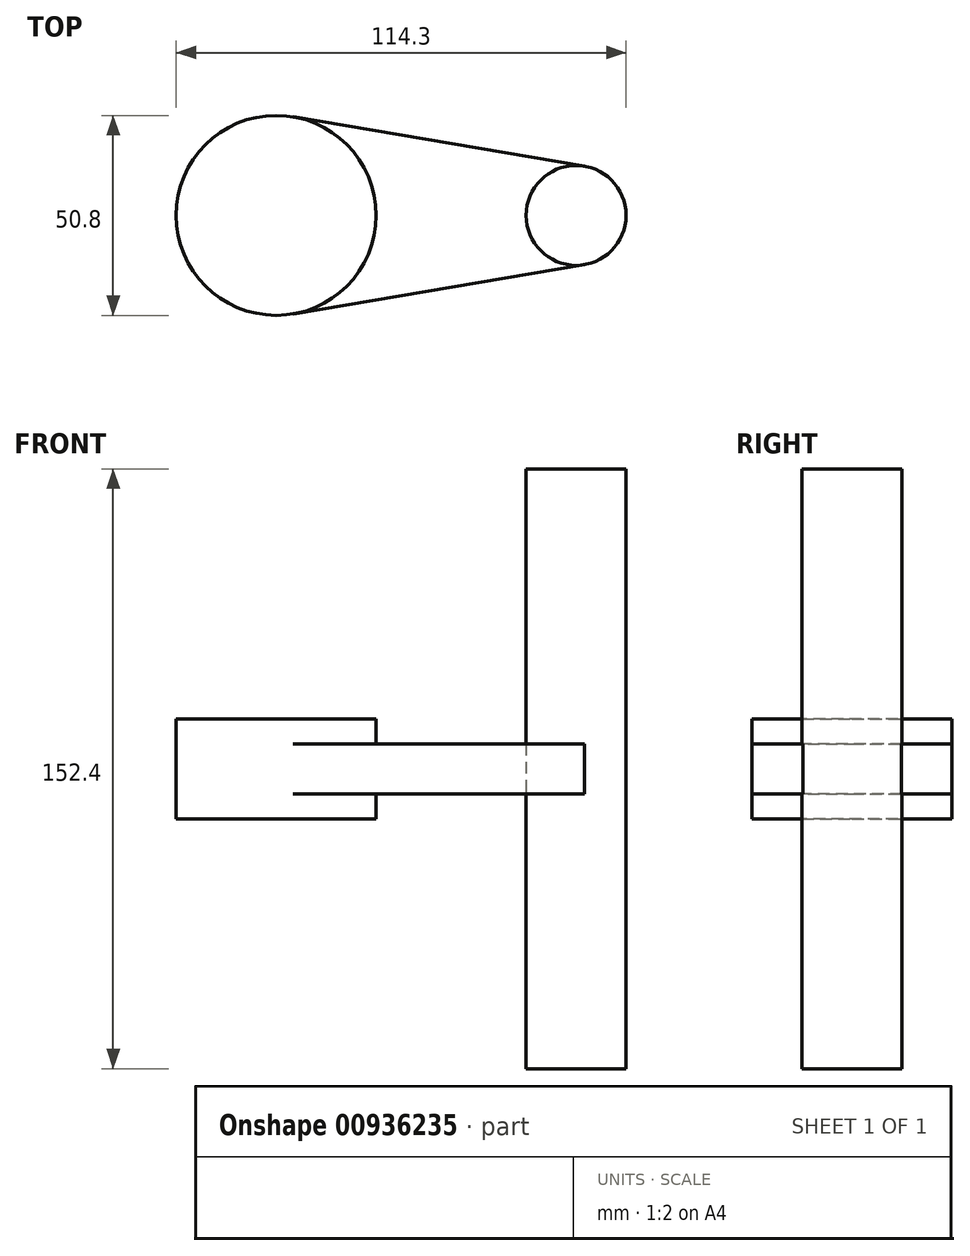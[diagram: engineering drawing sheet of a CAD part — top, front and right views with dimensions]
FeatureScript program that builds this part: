
annotation { "Feature Type Name" : "Feature", "Feature Type Description" : "" }
export const myFeature = defineFeature(function(context is Context, id is Id, definition is map)
    precondition{}
    {
        {
            var Q0;
            Q0=qCreatedBy(makeId("Top.planeOp"),FACE);
            var sketch = newSketch(context, id + "F0", { "sketchPlane" : qUnion([Q0])});
            skCircle(sketch, "E0", {"center": v(0, 0) * mm, "radius": 25.4 * mm});
            skCircle(sketch, "E1", {"center": v(76.2, 0) * mm, "radius": 12.7 * mm});
            skLineSegment(sketch, "E2", {"start": v(4.23, 25.04) * mm, "end": v(78.32, 12.52) * mm});
            skLineSegment(sketch, "E3.MirrorCS", {"start": v(4.23, -25.04) * mm, "end": v(78.32, -12.52) * mm});
            skSolve(sketch);
        }
        {
            var Q0;
            {var subQ0=sQuery(id+"F0.wireOp",EDGE,"E0");var subQ1=makeQuery(id+"F0.imprint","INTERSECT",VERTEX,{"derivedFrom":[subQ0,sQuery(id+"F0.wireOp",EDGE,"E2")]});Q0=makeQuery(id+"F0.imprint","IMPRINT",FACE,{"disambiguationData":[TD([[makeQuery(id+"F0.imprint","IMPRINT",EDGE,{"disambiguationData":[TD([[subQ1,-1.0]])],"derivedFrom":subQ0}),1.0]])]});}
            extrude(context, id + "F1", {"entities" : qUnion([Q0]), "endBound" : BoundingType.SYMMETRIC, "depth" : 25.4 * mm, "offsetDistance" : 25.4 * mm});
        }
        {
            var Q0;
            {var subQ0=sQuery(id+"F0.wireOp",EDGE,"E2");Q0=makeQuery(id+"F0.imprint","IMPRINT",FACE,{"disambiguationData":[TD([[makeQuery(id+"F0.imprint","IMPRINT",EDGE,{"derivedFrom":subQ0}),-1.0]])]});}
            extrude(context, id + "F2", {"entities" : qUnion([Q0]), "operationType" : NewBodyOperationType.ADD, "endBound" : BoundingType.SYMMETRIC, "depth" : 12.7 * mm, "offsetDistance" : 25.4 * mm});
        }
        {
            var Q0;
            {var subQ0=sQuery(id+"F0.wireOp",EDGE,"E1");var subQ1=makeQuery(id+"F0.imprint","INTERSECT",VERTEX,{"derivedFrom":[subQ0,sQuery(id+"F0.wireOp",EDGE,"E2")]});Q0=makeQuery(id+"F0.imprint","IMPRINT",FACE,{"disambiguationData":[TD([[makeQuery(id+"F0.imprint","IMPRINT",EDGE,{"disambiguationData":[TD([[subQ1,-1.0]])],"derivedFrom":subQ0}),1.0]])]});}
            extrude(context, id + "F3", {"entities" : qUnion([Q0]), "endBound" : BoundingType.SYMMETRIC, "depth" : 152.4 * mm, "offsetDistance" : 25.4 * mm});
        }
        {
            var Q0;
            Q0=makeQuery(id+"F1.opExtrude","CAP_FACE",FACE,{"disambiguationData":[OSD([sQuery(id+"F0.wireOp",EDGE,"E0")])],"isStart":false});
            cPlane(context, id + "F4", {"entities" : qUnion([Q0]), "cplaneType" : CPlaneType.OFFSET, "offset" : 0 * mm, "width" : 152.4 * mm, "height" : 152.4 * mm});
        }
        {
            var Q0;
            Q0=qCreatedBy(id+"F4.planeOp",FACE);
            var sketch = newSketch(context, id + "F5", { "sketchPlane" : qUnion([Q0])});
            skCircle(sketch, "E4", {"center": v(0, 0) * mm, "radius": 50.8 * mm});
            skSolve(sketch);
        }
        {
            var Q0;
            Q0=sQuery(id+"F5.wireOp",EDGE,"E4");
            extrude(context, id + "F6", {"bodyType" : ToolBodyType.SURFACE, "surfaceEntities" : qUnion([Q0]), "depth" : 12.7 * mm, "offsetDistance" : 25.4 * mm});
        }
    });
